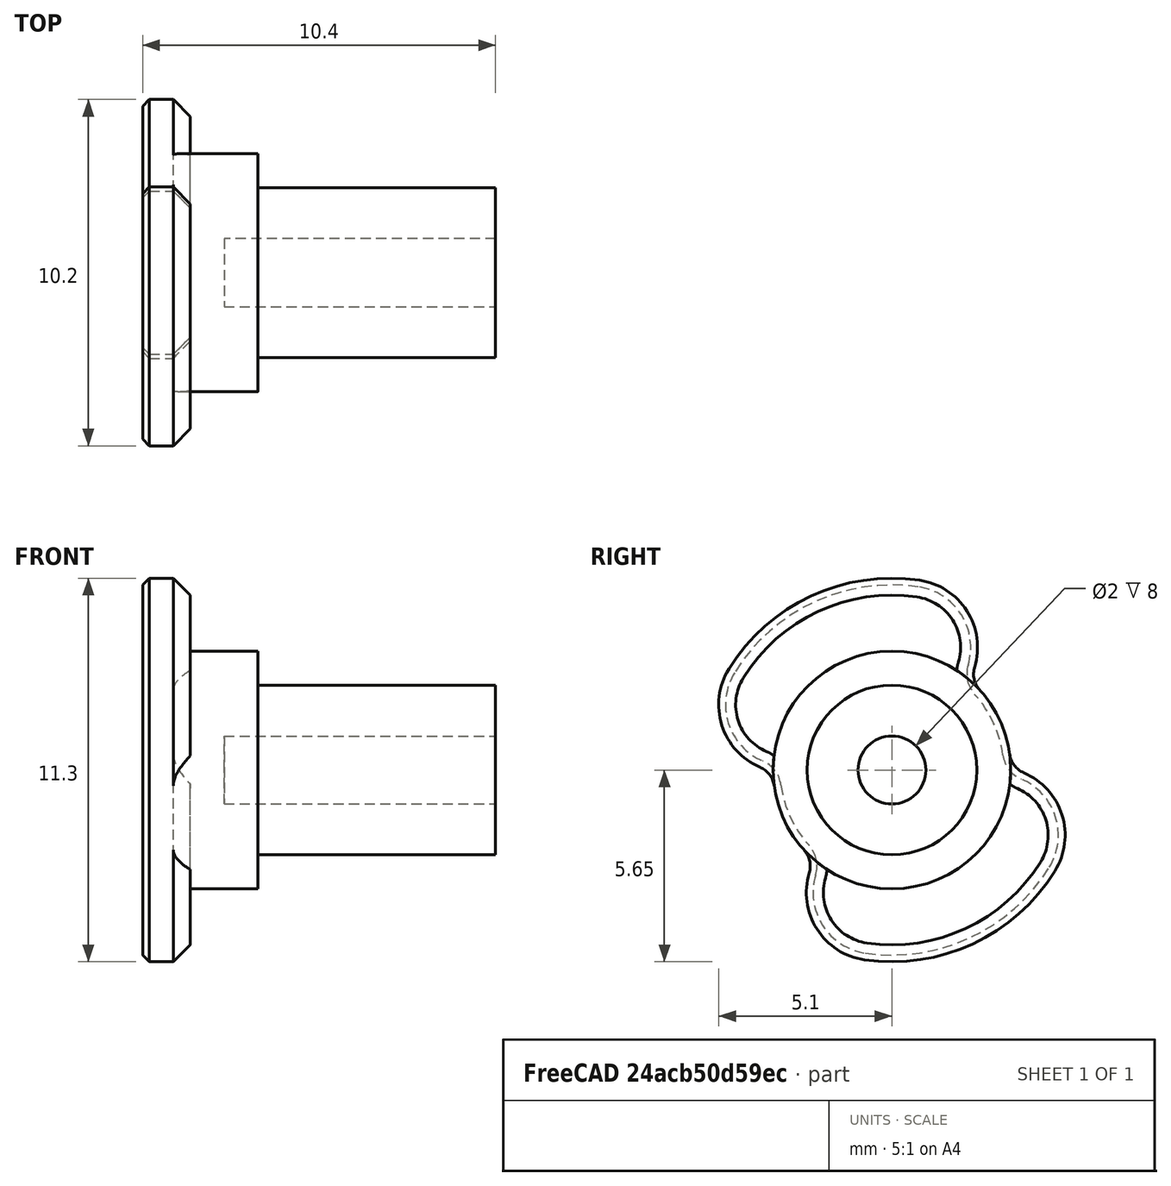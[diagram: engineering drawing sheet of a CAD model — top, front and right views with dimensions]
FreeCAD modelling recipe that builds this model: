
FCSTD DOCUMENT  (FreeCAD 0.18R)
Label: pillar-post
License: All rights reserved
LicenseURL: http://en.wikipedia.org/wiki/All_rights_reserved
objects: Sketcher::SketchObject×2, Part::Extrusion×2, Part::Cut×2, Part::Feature×1, Part::Box×1, Part::MultiCommon×1
note: 9 computed .brp shape members not serialized (recipe doc carries the construction recipe); baked Part::Feature solids carry a one-line shape summary decoded from their .brp

FEATURE [Part::Feature] Part__Feature  label="Left"
  shape: bbox 16.63 x 51.54 x 37.89 mm, 132 faces (baked)
FEATURE [Part::Box] Box  label="Cube"
  AttacherType = Attacher::AttachEngine3D
  Height = 50
  Length = 100
  Placement = pos=(-99.39,10,0) rot=(0,0,1;0rad)
  Width = 50
FEATURE [Part::MultiCommon] Common
  Shapes = -> [Part__Feature,Box]
FEATURE [Sketcher::SketchObject] Sketch
  ExternalGeometry = -> [Common]
  MapMode = 5
  Placement = pos=(0.61,0,0) rot=(0.57735,0.57735,0.57735;2.0944rad)
  Support = -> [Common]
  sketch-geometry (2):
    g0: Circle CenterX=27.3599 CenterY=15 CenterZ=0 NormalX=0 NormalY=0 NormalZ=1 AngleXU=0 Radius=2.5
    g1: Circle CenterX=27.3599 CenterY=15 CenterZ=0 NormalX=0 NormalY=0 NormalZ=1 AngleXU=0 Radius=15
  constraints (4):
    c: Coincident(g0,g-3)
    c: Coincident(g1,g0)
    c: Radius(g1) = 15
    c: Radius(g0) = 2.5
FEATURE [Part::Extrusion] Extrude
  Base = -> Sketch
  Dir = (1,0,0)
  DirMode = 2
  FaceMakerClass = Part::FaceMakerBullseye
  LengthFwd = -7
  LengthRev = 0
  Solid = true
  Symmetric = false
FEATURE [Part::Cut] Cut
  Base = -> Common
  Tool = -> Extrude
FEATURE [Sketcher::SketchObject] Sketch001
  ExternalGeometry = -> [Cut]
  MapMode = 5
  Placement = pos=(0.61,0,0) rot=(0.57735,0.57735,0.57735;2.0944rad)
  Support = -> [Cut001]
  sketch-geometry (1):
    g0: Circle CenterX=27.3599 CenterY=15 CenterZ=0 NormalX=0 NormalY=0 NormalZ=1 AngleXU=0 Radius=1
  constraints (2):
    c: Coincident(g0,g-3)
    c: Radius(g0) = 1
FEATURE [Part::Extrusion] Extrude001
  Base = -> Sketch001
  Dir = (1,0,0)
  DirMode = 2
  FaceMakerClass = Part::FaceMakerBullseye
  LengthFwd = -8
  LengthRev = 0
  Solid = true
  Symmetric = false
FEATURE [Part::Cut] Cut001
  Base = -> Cut
  Tool = -> Extrude001
